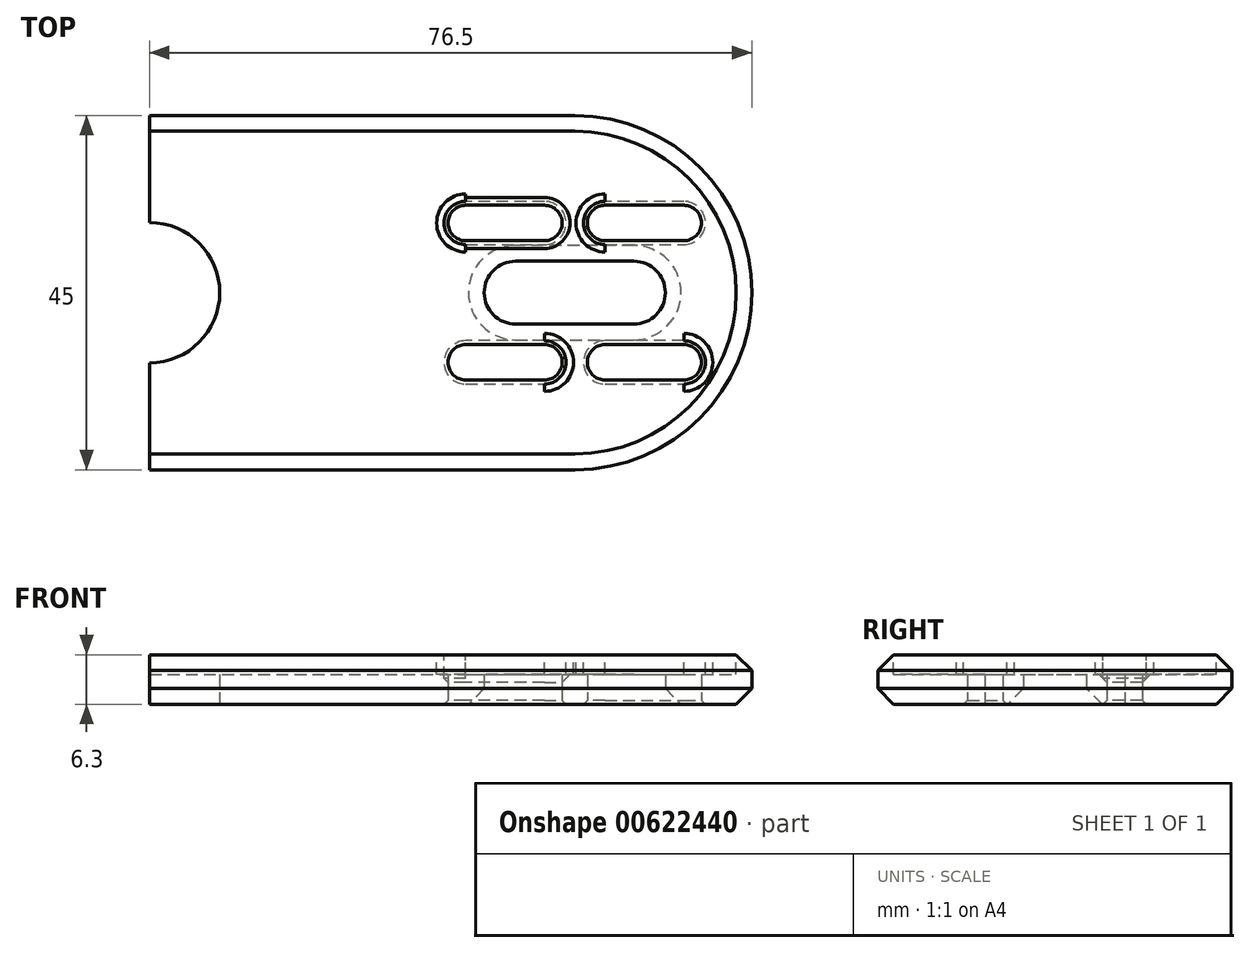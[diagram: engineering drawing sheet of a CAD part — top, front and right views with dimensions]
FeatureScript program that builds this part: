
annotation { "Feature Type Name" : "Feature", "Feature Type Description" : "" }
export const myFeature = defineFeature(function(context is Context, id is Id, definition is map)
    precondition{}
    {
        {
            var Q0;
            Q0=qCreatedBy(makeId("Top.planeOp"),FACE);
            var sketch = newSketch(context, id + "F0", { "sketchPlane" : qUnion([Q0])});
            skLineSegment(sketch, "E0.bottom", {"start": v(27, 22.5) * mm, "end": v(-27, 22.5) * mm});
            skLineSegment(sketch, "E0.top", {"start": v(27, -22.5) * mm, "end": v(-27, -22.5) * mm});
            skLineSegment(sketch, "E0.left", {"start": v(27, 22.5) * mm, "end": v(27, -22.5) * mm});
            skLineSegment(sketch, "E0.right", {"start": v(-27, 22.5) * mm, "end": v(-27, -22.5) * mm});
            skPoint(sketch, "E0.middle", {"position": v(0, 0) * mm});
            skArc(sketch, "E1", {"start": v(27, -22.5) * mm, "mid": v(49.5, 0) * mm, "end": v(27, 22.5) * mm});
            skArc(sketch, "E2", {"start": v(-27, -22.5) * mm, "mid": v(-49.5, 0) * mm, "end": v(-27, 22.5) * mm});
            skCircle(sketch, "E3", {"center": v(-27, 0) * mm, "radius": 8.9 * mm});
            skLineSegment(sketch, "E4.bottom", {"start": v(34.5, 4) * mm, "end": v(19.5, 4) * mm});
            skLineSegment(sketch, "E4.top", {"start": v(34.5, -4) * mm, "end": v(19.5, -4) * mm});
            skLineSegment(sketch, "E4.left", {"start": v(34.5, 4) * mm, "end": v(34.5, -4) * mm});
            skLineSegment(sketch, "E4.right", {"start": v(19.5, 4) * mm, "end": v(19.5, -4) * mm});
            skArc(sketch, "E5", {"start": v(34.5, -4) * mm, "mid": v(38.5, 0) * mm, "end": v(34.5, 4) * mm});
            skArc(sketch, "E6", {"start": v(19.5, -4) * mm, "mid": v(15.5, 0) * mm, "end": v(19.5, 4) * mm});
            skPoint(sketch, "E7.middle.positionSnap0", {"position": v(38.5, 0) * mm});
            skPoint(sketch, "E7.centerSnap0", {"position": v(38.5, 0) * mm});
            skPoint(sketch, "E8.middle.positionSnap0", {"position": v(15.5, 0) * mm});
            skPoint(sketch, "E8.centerSnap0", {"position": v(15.5, 0) * mm});
            skLineSegment(sketch, "E9.bottom", {"start": v(30.85, 11.1) * mm, "end": v(40.85, 11.1) * mm});
            skLineSegment(sketch, "E9.top", {"start": v(30.85, 6.6) * mm, "end": v(40.85, 6.6) * mm});
            skLineSegment(sketch, "E9.left", {"start": v(30.85, 11.1) * mm, "end": v(30.85, 6.6) * mm});
            skLineSegment(sketch, "E9.right", {"start": v(40.85, 11.1) * mm, "end": v(40.85, 6.6) * mm});
            skPoint(sketch, "E9.middle", {"position": v(35.85, 8.85) * mm});
            skLineSegment(sketch, "E10.bottom", {"start": v(13.15, 11.1) * mm, "end": v(23.15, 11.1) * mm});
            skLineSegment(sketch, "E10.top", {"start": v(13.15, 6.6) * mm, "end": v(23.15, 6.6) * mm});
            skLineSegment(sketch, "E10.left", {"start": v(13.15, 11.1) * mm, "end": v(13.15, 6.6) * mm});
            skLineSegment(sketch, "E10.right", {"start": v(23.15, 11.1) * mm, "end": v(23.15, 6.6) * mm});
            skPoint(sketch, "E10.middle", {"position": v(18.15, 8.85) * mm});
            skLineSegment(sketch, "E11.bottom", {"start": v(13.15, -11.1) * mm, "end": v(23.15, -11.1) * mm});
            skLineSegment(sketch, "E11.top", {"start": v(13.15, -6.6) * mm, "end": v(23.15, -6.6) * mm});
            skLineSegment(sketch, "E11.left", {"start": v(13.15, -11.1) * mm, "end": v(13.15, -6.6) * mm});
            skLineSegment(sketch, "E11.right", {"start": v(23.15, -11.1) * mm, "end": v(23.15, -6.6) * mm});
            skPoint(sketch, "E11.middle", {"position": v(18.15, -8.85) * mm});
            skLineSegment(sketch, "E12.bottom", {"start": v(30.85, -6.6) * mm, "end": v(40.85, -6.6) * mm});
            skLineSegment(sketch, "E12.top", {"start": v(30.85, -11.1) * mm, "end": v(40.85, -11.1) * mm});
            skLineSegment(sketch, "E12.left", {"start": v(30.85, -6.6) * mm, "end": v(30.85, -11.1) * mm});
            skLineSegment(sketch, "E12.right", {"start": v(40.85, -6.6) * mm, "end": v(40.85, -11.1) * mm});
            skPoint(sketch, "E12.middle", {"position": v(35.85, -8.85) * mm});
            skArc(sketch, "E13", {"start": v(13.15, 6.6) * mm, "mid": v(10.9, 8.85) * mm, "end": v(13.15, 11.1) * mm});
            skArc(sketch, "E14", {"start": v(23.15, 11.1) * mm, "mid": v(25.4, 8.85) * mm, "end": v(23.15, 6.6) * mm});
            skArc(sketch, "E15", {"start": v(30.85, 6.6) * mm, "mid": v(28.6, 8.85) * mm, "end": v(30.85, 11.1) * mm});
            skArc(sketch, "E16", {"start": v(40.85, 11.1) * mm, "mid": v(43.1, 8.85) * mm, "end": v(40.85, 6.6) * mm});
            skArc(sketch, "E17", {"start": v(23.15, -11.1) * mm, "mid": v(25.4, -8.85) * mm, "end": v(23.15, -6.6) * mm});
            skArc(sketch, "E18", {"start": v(13.15, -11.1) * mm, "mid": v(10.9, -8.85) * mm, "end": v(13.15, -6.6) * mm});
            skArc(sketch, "E19", {"start": v(30.85, -11.1) * mm, "mid": v(28.6, -8.85) * mm, "end": v(30.85, -6.6) * mm});
            skArc(sketch, "E20", {"start": v(40.85, -11.1) * mm, "mid": v(43.1, -8.85) * mm, "end": v(40.85, -6.6) * mm});
            skSolve(sketch);
        }
        {
            var Q0;
            {var subQ1=sQuery(id+"F0.wireOp",EDGE,"E1");Q0=makeQuery(id+"F0.imprint","IMPRINT",FACE,{"disambiguationData":[TD([[makeQuery(id+"F0.imprint","IMPRINT",EDGE,{"derivedFrom":subQ1}),1.0]])]});}
            var Q1;
            {var subQ6=sQuery(id+"F0.wireOp",EDGE,"E0.bottom");Q1=makeQuery(id+"F0.imprint","IMPRINT",FACE,{"disambiguationData":[TD([[makeQuery(id+"F0.imprint","IMPRINT",EDGE,{"derivedFrom":subQ6}),1.0]])]});}
            var Q2;
            {var subQ0=sQuery(id+"F0.wireOp",EDGE,"E2");Q2=makeQuery(id+"F0.imprint","IMPRINT",FACE,{"disambiguationData":[TD([[makeQuery(id+"F0.imprint","IMPRINT",EDGE,{"derivedFrom":subQ0}),-1.0]])]});}
            extrude(context, id + "F1", {"entities" : qUnion([Q0, Q1, Q2]), "depth" : 6.3 * mm, "offsetDistance" : 25 * mm});
        }
        {
            var Q0;
            Q0=makeQuery(id+"F1.opExtrude","CAP_EDGE",EDGE,{"disambiguationData":[OSD([sQuery(id+"F0.wireOp",EDGE,"E10.bottom")])],"isStart":false});
            var Q1;
            Q1=makeQuery(id+"F1.opExtrude","CAP_EDGE",EDGE,{"disambiguationData":[OSD([sQuery(id+"F0.wireOp",EDGE,"E9.bottom")])],"isStart":false});
            var Q2;
            Q2=makeQuery(id+"F1.opExtrude","CAP_EDGE",EDGE,{"disambiguationData":[OSD([sQuery(id+"F0.wireOp",EDGE,"E12.bottom")])],"isStart":false});
            var Q3;
            Q3=makeQuery(id+"F1.opExtrude","CAP_EDGE",EDGE,{"disambiguationData":[OSD([sQuery(id+"F0.wireOp",EDGE,"E11.top")])],"isStart":false});
            var Q4;
            Q4=makeQuery(id+"F1.opExtrude","CAP_EDGE",EDGE,{"disambiguationData":[OSD([sQuery(id+"F0.wireOp",EDGE,"E9.bottom")])],"isStart":true});
            var Q5;
            Q5=makeQuery(id+"F1.opExtrude","CAP_EDGE",EDGE,{"disambiguationData":[OSD([sQuery(id+"F0.wireOp",EDGE,"E10.bottom")])],"isStart":true});
            var Q6;
            Q6=makeQuery(id+"F1.opExtrude","CAP_EDGE",EDGE,{"disambiguationData":[OSD([sQuery(id+"F0.wireOp",EDGE,"E12.bottom")])],"isStart":true});
            var Q7;
            Q7=makeQuery(id+"F1.opExtrude","CAP_EDGE",EDGE,{"disambiguationData":[OSD([sQuery(id+"F0.wireOp",EDGE,"E11.top")])],"isStart":true});
            chamfer(context, id + "F2", {"entities" : qUnion([Q0, Q1, Q2, Q3, Q4, Q5, Q6, Q7]), "width" : .5 * mm, "tangentPropagation" : true});
        }
        {
            var Q0;
            Q0=makeQuery(id+"F1.opExtrude","CAP_EDGE",EDGE,{"disambiguationData":[OSD([sQuery(id+"F0.wireOp",EDGE,"E0.top")])],"isStart":false});
            var Q1;
            Q1=makeQuery(id+"F1.opExtrude","CAP_EDGE",EDGE,{"disambiguationData":[OSD([sQuery(id+"F0.wireOp",EDGE,"E0.top")])],"isStart":true});
            chamfer(context, id + "F3", {"entities" : qUnion([Q0, Q1]), "width" : 2 * mm, "tangentPropagation" : true});
        }
        {
            var Q0;
            Q0=makeQuery(id+"F1.opExtrude","CAP_FACE",FACE,{"disambiguationData":[OSD([sQuery(id+"F0.wireOp",EDGE,"E0.bottom"),sQuery(id+"F0.wireOp",EDGE,"E0.top"),sQuery(id+"F0.wireOp",EDGE,"E1"),sQuery(id+"F0.wireOp",EDGE,"E2"),sQuery(id+"F0.wireOp",EDGE,"E3"),sQuery(id+"F0.wireOp",EDGE,"E4.bottom"),sQuery(id+"F0.wireOp",EDGE,"E4.top"),sQuery(id+"F0.wireOp",EDGE,"E5"),sQuery(id+"F0.wireOp",EDGE,"E6"),sQuery(id+"F0.wireOp",EDGE,"E9.bottom"),sQuery(id+"F0.wireOp",EDGE,"E9.top"),sQuery(id+"F0.wireOp",EDGE,"E10.bottom"),sQuery(id+"F0.wireOp",EDGE,"E10.top"),sQuery(id+"F0.wireOp",EDGE,"E11.bottom"),sQuery(id+"F0.wireOp",EDGE,"E11.top"),sQuery(id+"F0.wireOp",EDGE,"E12.bottom"),sQuery(id+"F0.wireOp",EDGE,"E12.top"),sQuery(id+"F0.wireOp",EDGE,"E13"),sQuery(id+"F0.wireOp",EDGE,"E14"),sQuery(id+"F0.wireOp",EDGE,"E15"),sQuery(id+"F0.wireOp",EDGE,"E16"),sQuery(id+"F0.wireOp",EDGE,"E17"),sQuery(id+"F0.wireOp",EDGE,"E18"),sQuery(id+"F0.wireOp",EDGE,"E19"),sQuery(id+"F0.wireOp",EDGE,"E20")])],"isStart":false});
            var sketch = newSketch(context, id + "F4", { "sketchPlane" : qUnion([Q0])});
            skLineSegment(sketch, "E21.bottom", {"start": v(13.15, 12.54) * mm, "end": v(23.15, 12.54) * mm});
            skLineSegment(sketch, "E21.top", {"start": v(13.15, 5.16) * mm, "end": v(23.15, 5.16) * mm});
            skLineSegment(sketch, "E21.left", {"start": v(13.15, 12.54) * mm, "end": v(13.15, 5.16) * mm});
            skLineSegment(sketch, "E21.right", {"start": v(23.15, 12.54) * mm, "end": v(23.15, 5.16) * mm});
            skArc(sketch, "E22", {"start": v(13.15, 5.16) * mm, "mid": v(9.46, 8.85) * mm, "end": v(13.15, 12.54) * mm});
            skArc(sketch, "E23", {"start": v(23.15, 5.16) * mm, "mid": v(26.84, 8.85) * mm, "end": v(23.15, 12.54) * mm});
            skLineSegment(sketch, "E24.MirrorCS", {"start": v(40.85, 5.16) * mm, "end": v(30.85, 5.16) * mm});
            skLineSegment(sketch, "E25.MirrorCS", {"start": v(40.85, 12.54) * mm, "end": v(40.85, 5.16) * mm});
            skArc(sketch, "E26.MirrorCS", {"start": v(40.85, 5.16) * mm, "mid": v(44.54, 8.85) * mm, "end": v(40.85, 12.54) * mm});
            skArc(sketch, "E27.MirrorCS", {"start": v(30.85, 5.16) * mm, "mid": v(27.16, 8.85) * mm, "end": v(30.85, 12.54) * mm});
            skLineSegment(sketch, "E28.MirrorCS", {"start": v(40.85, 12.54) * mm, "end": v(30.85, 12.54) * mm});
            skLineSegment(sketch, "E29.MirrorCS", {"start": v(30.85, 12.54) * mm, "end": v(30.85, 5.16) * mm});
            skLineSegment(sketch, "E30.MirrorCS", {"start": v(40.85, -12.54) * mm, "end": v(40.85, -5.16) * mm});
            skLineSegment(sketch, "E31.MirrorCS", {"start": v(40.85, -12.54) * mm, "end": v(30.85, -12.54) * mm});
            skLineSegment(sketch, "E32.MirrorCS", {"start": v(23.15, -12.54) * mm, "end": v(23.15, -5.16) * mm});
            skLineSegment(sketch, "E33.MirrorCS", {"start": v(30.85, -12.54) * mm, "end": v(30.85, -5.16) * mm});
            skArc(sketch, "E34.MirrorCS", {"start": v(13.15, -5.16) * mm, "mid": v(9.46, -8.85) * mm, "end": v(13.15, -12.54) * mm});
            skLineSegment(sketch, "E35.MirrorCS", {"start": v(13.15, -12.54) * mm, "end": v(13.15, -5.16) * mm});
            skLineSegment(sketch, "E36.MirrorCS", {"start": v(13.15, -5.16) * mm, "end": v(23.15, -5.16) * mm});
            skArc(sketch, "E37.MirrorCS", {"start": v(40.85, -5.16) * mm, "mid": v(44.54, -8.85) * mm, "end": v(40.85, -12.54) * mm});
            skLineSegment(sketch, "E38.MirrorCS", {"start": v(40.85, -5.16) * mm, "end": v(30.85, -5.16) * mm});
            skLineSegment(sketch, "E39.MirrorCS", {"start": v(13.15, -12.54) * mm, "end": v(23.15, -12.54) * mm});
            skArc(sketch, "E40.MirrorCS", {"start": v(30.85, -5.16) * mm, "mid": v(27.16, -8.85) * mm, "end": v(30.85, -12.54) * mm});
            skArc(sketch, "E41.MirrorCS", {"start": v(23.15, -5.16) * mm, "mid": v(26.84, -8.85) * mm, "end": v(23.15, -12.54) * mm});
            skSolve(sketch);
        }
        {
            var Q0;
            {var subQ0=sQuery(id+"F4.wireOp",EDGE,"E21.bottom");Q0=makeQuery(id+"F4.imprint","IMPRINT",FACE,{"disambiguationData":[TD([[makeQuery(id+"F4.imprint","IMPRINT",EDGE,{"derivedFrom":subQ0}),-1.0]])]});}
            var Q1;
            {var subQ6=sQuery(id+"F4.wireOp",EDGE,"E22");Q1=makeQuery(id+"F4.imprint","IMPRINT",FACE,{"disambiguationData":[TD([[makeQuery(id+"F4.imprint","IMPRINT",EDGE,{"derivedFrom":subQ6}),-1.0]])]});}
            var Q2;
            {var subQ1=sQuery(id+"F0.wireOp",EDGE,"E13");var subQ2=sQuery(id+"F0.wireOp",EDGE,"E10.top");var subQ3=sQuery(id+"F0.wireOp",EDGE,"E10.bottom");var subQ4=makeQuery(id+"F1.opExtrude","CAP_FACE",FACE,{"disambiguationData":[OSD([sQuery(id+"F0.wireOp",EDGE,"E0.bottom"),sQuery(id+"F0.wireOp",EDGE,"E0.top"),sQuery(id+"F0.wireOp",EDGE,"E1"),sQuery(id+"F0.wireOp",EDGE,"E2"),sQuery(id+"F0.wireOp",EDGE,"E3"),sQuery(id+"F0.wireOp",EDGE,"E4.bottom"),sQuery(id+"F0.wireOp",EDGE,"E4.top"),sQuery(id+"F0.wireOp",EDGE,"E5"),sQuery(id+"F0.wireOp",EDGE,"E6"),sQuery(id+"F0.wireOp",EDGE,"E9.bottom"),sQuery(id+"F0.wireOp",EDGE,"E9.top"),subQ3,subQ2,sQuery(id+"F0.wireOp",EDGE,"E11.bottom"),sQuery(id+"F0.wireOp",EDGE,"E11.top"),sQuery(id+"F0.wireOp",EDGE,"E12.bottom"),sQuery(id+"F0.wireOp",EDGE,"E12.top"),subQ1,sQuery(id+"F0.wireOp",EDGE,"E14"),sQuery(id+"F0.wireOp",EDGE,"E15"),sQuery(id+"F0.wireOp",EDGE,"E16"),sQuery(id+"F0.wireOp",EDGE,"E17"),sQuery(id+"F0.wireOp",EDGE,"E18"),sQuery(id+"F0.wireOp",EDGE,"E19"),sQuery(id+"F0.wireOp",EDGE,"E20")])],"isStart":false});var subQ5=makeQuery(id+"F2.opChamfer","BLEND_EDGE",EDGE,{"blendedFrom":[makeQuery(id+"F1.opExtrude","CAP_EDGE",EDGE,{"disambiguationData":[OSD([subQ1])],"isStart":false}),subQ4],"blendedInto":[subQ4]});Q2=makeQuery(id+"F4.imprint","IMPRINT",FACE,{"disambiguationData":[TD([[makeQuery(id+"F4.imprint","IMPRINT",EDGE,{"derivedFrom":subQ5}),-1.0]])]});}
            var Q3;
            {var subQ1=sQuery(id+"F0.wireOp",EDGE,"E14");var subQ2=sQuery(id+"F0.wireOp",EDGE,"E13");var subQ3=sQuery(id+"F0.wireOp",EDGE,"E10.top");var subQ4=sQuery(id+"F0.wireOp",EDGE,"E10.bottom");var subQ5=makeQuery(id+"F1.opExtrude","CAP_FACE",FACE,{"disambiguationData":[OSD([sQuery(id+"F0.wireOp",EDGE,"E0.bottom"),sQuery(id+"F0.wireOp",EDGE,"E0.top"),sQuery(id+"F0.wireOp",EDGE,"E1"),sQuery(id+"F0.wireOp",EDGE,"E2"),sQuery(id+"F0.wireOp",EDGE,"E3"),sQuery(id+"F0.wireOp",EDGE,"E4.bottom"),sQuery(id+"F0.wireOp",EDGE,"E4.top"),sQuery(id+"F0.wireOp",EDGE,"E5"),sQuery(id+"F0.wireOp",EDGE,"E6"),sQuery(id+"F0.wireOp",EDGE,"E9.bottom"),sQuery(id+"F0.wireOp",EDGE,"E9.top"),subQ4,subQ3,sQuery(id+"F0.wireOp",EDGE,"E11.bottom"),sQuery(id+"F0.wireOp",EDGE,"E11.top"),sQuery(id+"F0.wireOp",EDGE,"E12.bottom"),sQuery(id+"F0.wireOp",EDGE,"E12.top"),subQ2,subQ1,sQuery(id+"F0.wireOp",EDGE,"E15"),sQuery(id+"F0.wireOp",EDGE,"E16"),sQuery(id+"F0.wireOp",EDGE,"E17"),sQuery(id+"F0.wireOp",EDGE,"E18"),sQuery(id+"F0.wireOp",EDGE,"E19"),sQuery(id+"F0.wireOp",EDGE,"E20")])],"isStart":false});var subQ7=makeQuery(id+"F2.opChamfer","BLEND_EDGE",EDGE,{"blendedFrom":[makeQuery(id+"F1.opExtrude","CAP_EDGE",EDGE,{"disambiguationData":[OSD([subQ4])],"isStart":false}),subQ5],"blendedInto":[subQ5]});Q3=makeQuery(id+"F4.imprint","IMPRINT",FACE,{"disambiguationData":[TD([[makeQuery(id+"F4.imprint","IMPRINT",EDGE,{"derivedFrom":subQ7}),-1.0]])]});}
            var Q4;
            {var subQ0=sQuery(id+"F4.wireOp",EDGE,"E21.top");Q4=makeQuery(id+"F4.imprint","IMPRINT",FACE,{"disambiguationData":[TD([[makeQuery(id+"F4.imprint","IMPRINT",EDGE,{"derivedFrom":subQ0}),1.0]])]});}
            var Q5;
            {var subQ1=sQuery(id+"F0.wireOp",EDGE,"E14");var subQ2=sQuery(id+"F0.wireOp",EDGE,"E10.top");var subQ3=sQuery(id+"F0.wireOp",EDGE,"E10.bottom");var subQ4=makeQuery(id+"F1.opExtrude","CAP_FACE",FACE,{"disambiguationData":[OSD([sQuery(id+"F0.wireOp",EDGE,"E0.bottom"),sQuery(id+"F0.wireOp",EDGE,"E0.top"),sQuery(id+"F0.wireOp",EDGE,"E1"),sQuery(id+"F0.wireOp",EDGE,"E2"),sQuery(id+"F0.wireOp",EDGE,"E3"),sQuery(id+"F0.wireOp",EDGE,"E4.bottom"),sQuery(id+"F0.wireOp",EDGE,"E4.top"),sQuery(id+"F0.wireOp",EDGE,"E5"),sQuery(id+"F0.wireOp",EDGE,"E6"),sQuery(id+"F0.wireOp",EDGE,"E9.bottom"),sQuery(id+"F0.wireOp",EDGE,"E9.top"),subQ3,subQ2,sQuery(id+"F0.wireOp",EDGE,"E11.bottom"),sQuery(id+"F0.wireOp",EDGE,"E11.top"),sQuery(id+"F0.wireOp",EDGE,"E12.bottom"),sQuery(id+"F0.wireOp",EDGE,"E12.top"),sQuery(id+"F0.wireOp",EDGE,"E13"),subQ1,sQuery(id+"F0.wireOp",EDGE,"E15"),sQuery(id+"F0.wireOp",EDGE,"E16"),sQuery(id+"F0.wireOp",EDGE,"E17"),sQuery(id+"F0.wireOp",EDGE,"E18"),sQuery(id+"F0.wireOp",EDGE,"E19"),sQuery(id+"F0.wireOp",EDGE,"E20")])],"isStart":false});var subQ5=makeQuery(id+"F2.opChamfer","BLEND_EDGE",EDGE,{"blendedFrom":[makeQuery(id+"F1.opExtrude","CAP_EDGE",EDGE,{"disambiguationData":[OSD([subQ1])],"isStart":false}),subQ4],"blendedInto":[subQ4]});Q5=makeQuery(id+"F4.imprint","IMPRINT",FACE,{"disambiguationData":[TD([[makeQuery(id+"F4.imprint","IMPRINT",EDGE,{"derivedFrom":subQ5}),-1.0]])]});}
            var Q6;
            {var subQ6=sQuery(id+"F4.wireOp",EDGE,"E23");Q6=makeQuery(id+"F4.imprint","IMPRINT",FACE,{"disambiguationData":[TD([[makeQuery(id+"F4.imprint","IMPRINT",EDGE,{"derivedFrom":subQ6}),1.0]])]});}
            var Q7;
            {var subQ0=sQuery(id+"F4.wireOp",EDGE,"E27.MirrorCS");Q7=makeQuery(id+"F4.imprint","IMPRINT",FACE,{"disambiguationData":[TD([[makeQuery(id+"F4.imprint","IMPRINT",EDGE,{"derivedFrom":subQ0}),-1.0]])]});}
            var Q8;
            {var subQ1=sQuery(id+"F0.wireOp",EDGE,"E15");var subQ2=sQuery(id+"F0.wireOp",EDGE,"E9.top");var subQ3=sQuery(id+"F0.wireOp",EDGE,"E9.bottom");var subQ4=makeQuery(id+"F1.opExtrude","CAP_FACE",FACE,{"disambiguationData":[OSD([sQuery(id+"F0.wireOp",EDGE,"E0.bottom"),sQuery(id+"F0.wireOp",EDGE,"E0.top"),sQuery(id+"F0.wireOp",EDGE,"E1"),sQuery(id+"F0.wireOp",EDGE,"E2"),sQuery(id+"F0.wireOp",EDGE,"E3"),sQuery(id+"F0.wireOp",EDGE,"E4.bottom"),sQuery(id+"F0.wireOp",EDGE,"E4.top"),sQuery(id+"F0.wireOp",EDGE,"E5"),sQuery(id+"F0.wireOp",EDGE,"E6"),subQ3,subQ2,sQuery(id+"F0.wireOp",EDGE,"E10.bottom"),sQuery(id+"F0.wireOp",EDGE,"E10.top"),sQuery(id+"F0.wireOp",EDGE,"E11.bottom"),sQuery(id+"F0.wireOp",EDGE,"E11.top"),sQuery(id+"F0.wireOp",EDGE,"E12.bottom"),sQuery(id+"F0.wireOp",EDGE,"E12.top"),sQuery(id+"F0.wireOp",EDGE,"E13"),sQuery(id+"F0.wireOp",EDGE,"E14"),subQ1,sQuery(id+"F0.wireOp",EDGE,"E16"),sQuery(id+"F0.wireOp",EDGE,"E17"),sQuery(id+"F0.wireOp",EDGE,"E18"),sQuery(id+"F0.wireOp",EDGE,"E19"),sQuery(id+"F0.wireOp",EDGE,"E20")])],"isStart":false});var subQ5=makeQuery(id+"F2.opChamfer","BLEND_EDGE",EDGE,{"blendedFrom":[makeQuery(id+"F1.opExtrude","CAP_EDGE",EDGE,{"disambiguationData":[OSD([subQ1])],"isStart":false}),subQ4],"blendedInto":[subQ4]});Q8=makeQuery(id+"F4.imprint","IMPRINT",FACE,{"disambiguationData":[TD([[makeQuery(id+"F4.imprint","IMPRINT",EDGE,{"derivedFrom":subQ5}),-1.0]])]});}
            var Q9;
            {var subQ1=sQuery(id+"F0.wireOp",EDGE,"E16");var subQ2=sQuery(id+"F0.wireOp",EDGE,"E15");var subQ3=sQuery(id+"F0.wireOp",EDGE,"E9.top");var subQ4=sQuery(id+"F0.wireOp",EDGE,"E9.bottom");var subQ5=makeQuery(id+"F1.opExtrude","CAP_FACE",FACE,{"disambiguationData":[OSD([sQuery(id+"F0.wireOp",EDGE,"E0.bottom"),sQuery(id+"F0.wireOp",EDGE,"E0.top"),sQuery(id+"F0.wireOp",EDGE,"E1"),sQuery(id+"F0.wireOp",EDGE,"E2"),sQuery(id+"F0.wireOp",EDGE,"E3"),sQuery(id+"F0.wireOp",EDGE,"E4.bottom"),sQuery(id+"F0.wireOp",EDGE,"E4.top"),sQuery(id+"F0.wireOp",EDGE,"E5"),sQuery(id+"F0.wireOp",EDGE,"E6"),subQ4,subQ3,sQuery(id+"F0.wireOp",EDGE,"E10.bottom"),sQuery(id+"F0.wireOp",EDGE,"E10.top"),sQuery(id+"F0.wireOp",EDGE,"E11.bottom"),sQuery(id+"F0.wireOp",EDGE,"E11.top"),sQuery(id+"F0.wireOp",EDGE,"E12.bottom"),sQuery(id+"F0.wireOp",EDGE,"E12.top"),sQuery(id+"F0.wireOp",EDGE,"E13"),sQuery(id+"F0.wireOp",EDGE,"E14"),subQ2,subQ1,sQuery(id+"F0.wireOp",EDGE,"E17"),sQuery(id+"F0.wireOp",EDGE,"E18"),sQuery(id+"F0.wireOp",EDGE,"E19"),sQuery(id+"F0.wireOp",EDGE,"E20")])],"isStart":false});var subQ7=makeQuery(id+"F2.opChamfer","BLEND_EDGE",EDGE,{"blendedFrom":[makeQuery(id+"F1.opExtrude","CAP_EDGE",EDGE,{"disambiguationData":[OSD([subQ4])],"isStart":false}),subQ5],"blendedInto":[subQ5]});Q9=makeQuery(id+"F4.imprint","IMPRINT",FACE,{"disambiguationData":[TD([[makeQuery(id+"F4.imprint","IMPRINT",EDGE,{"derivedFrom":subQ7}),-1.0]])]});}
            var Q10;
            {var subQ6=sQuery(id+"F4.wireOp",EDGE,"E28.MirrorCS");Q10=makeQuery(id+"F4.imprint","IMPRINT",FACE,{"disambiguationData":[TD([[makeQuery(id+"F4.imprint","IMPRINT",EDGE,{"derivedFrom":subQ6}),1.0]])]});}
            var Q11;
            {var subQ0=sQuery(id+"F4.wireOp",EDGE,"E24.MirrorCS");Q11=makeQuery(id+"F4.imprint","IMPRINT",FACE,{"disambiguationData":[TD([[makeQuery(id+"F4.imprint","IMPRINT",EDGE,{"derivedFrom":subQ0}),-1.0]])]});}
            var Q12;
            {var subQ6=sQuery(id+"F4.wireOp",EDGE,"E26.MirrorCS");Q12=makeQuery(id+"F4.imprint","IMPRINT",FACE,{"disambiguationData":[TD([[makeQuery(id+"F4.imprint","IMPRINT",EDGE,{"derivedFrom":subQ6}),1.0]])]});}
            var Q13;
            {var subQ1=sQuery(id+"F0.wireOp",EDGE,"E16");var subQ2=sQuery(id+"F0.wireOp",EDGE,"E9.top");var subQ3=sQuery(id+"F0.wireOp",EDGE,"E9.bottom");var subQ4=makeQuery(id+"F1.opExtrude","CAP_FACE",FACE,{"disambiguationData":[OSD([sQuery(id+"F0.wireOp",EDGE,"E0.bottom"),sQuery(id+"F0.wireOp",EDGE,"E0.top"),sQuery(id+"F0.wireOp",EDGE,"E1"),sQuery(id+"F0.wireOp",EDGE,"E2"),sQuery(id+"F0.wireOp",EDGE,"E3"),sQuery(id+"F0.wireOp",EDGE,"E4.bottom"),sQuery(id+"F0.wireOp",EDGE,"E4.top"),sQuery(id+"F0.wireOp",EDGE,"E5"),sQuery(id+"F0.wireOp",EDGE,"E6"),subQ3,subQ2,sQuery(id+"F0.wireOp",EDGE,"E10.bottom"),sQuery(id+"F0.wireOp",EDGE,"E10.top"),sQuery(id+"F0.wireOp",EDGE,"E11.bottom"),sQuery(id+"F0.wireOp",EDGE,"E11.top"),sQuery(id+"F0.wireOp",EDGE,"E12.bottom"),sQuery(id+"F0.wireOp",EDGE,"E12.top"),sQuery(id+"F0.wireOp",EDGE,"E13"),sQuery(id+"F0.wireOp",EDGE,"E14"),sQuery(id+"F0.wireOp",EDGE,"E15"),subQ1,sQuery(id+"F0.wireOp",EDGE,"E17"),sQuery(id+"F0.wireOp",EDGE,"E18"),sQuery(id+"F0.wireOp",EDGE,"E19"),sQuery(id+"F0.wireOp",EDGE,"E20")])],"isStart":false});var subQ5=makeQuery(id+"F2.opChamfer","BLEND_EDGE",EDGE,{"blendedFrom":[makeQuery(id+"F1.opExtrude","CAP_EDGE",EDGE,{"disambiguationData":[OSD([subQ1])],"isStart":false}),subQ4],"blendedInto":[subQ4]});Q13=makeQuery(id+"F4.imprint","IMPRINT",FACE,{"disambiguationData":[TD([[makeQuery(id+"F4.imprint","IMPRINT",EDGE,{"derivedFrom":subQ5}),-1.0]])]});}
            var Q14;
            {var subQ1=sQuery(id+"F0.wireOp",EDGE,"E18");var subQ2=sQuery(id+"F0.wireOp",EDGE,"E17");var subQ3=sQuery(id+"F0.wireOp",EDGE,"E11.top");var subQ4=sQuery(id+"F0.wireOp",EDGE,"E11.bottom");var subQ5=makeQuery(id+"F1.opExtrude","CAP_FACE",FACE,{"disambiguationData":[OSD([sQuery(id+"F0.wireOp",EDGE,"E0.bottom"),sQuery(id+"F0.wireOp",EDGE,"E0.top"),sQuery(id+"F0.wireOp",EDGE,"E1"),sQuery(id+"F0.wireOp",EDGE,"E2"),sQuery(id+"F0.wireOp",EDGE,"E3"),sQuery(id+"F0.wireOp",EDGE,"E4.bottom"),sQuery(id+"F0.wireOp",EDGE,"E4.top"),sQuery(id+"F0.wireOp",EDGE,"E5"),sQuery(id+"F0.wireOp",EDGE,"E6"),sQuery(id+"F0.wireOp",EDGE,"E9.bottom"),sQuery(id+"F0.wireOp",EDGE,"E9.top"),sQuery(id+"F0.wireOp",EDGE,"E10.bottom"),sQuery(id+"F0.wireOp",EDGE,"E10.top"),subQ4,subQ3,sQuery(id+"F0.wireOp",EDGE,"E12.bottom"),sQuery(id+"F0.wireOp",EDGE,"E12.top"),sQuery(id+"F0.wireOp",EDGE,"E13"),sQuery(id+"F0.wireOp",EDGE,"E14"),sQuery(id+"F0.wireOp",EDGE,"E15"),sQuery(id+"F0.wireOp",EDGE,"E16"),subQ2,subQ1,sQuery(id+"F0.wireOp",EDGE,"E19"),sQuery(id+"F0.wireOp",EDGE,"E20")])],"isStart":false});var subQ7=makeQuery(id+"F2.opChamfer","BLEND_EDGE",EDGE,{"blendedFrom":[makeQuery(id+"F1.opExtrude","CAP_EDGE",EDGE,{"disambiguationData":[OSD([subQ4])],"isStart":false}),subQ5],"blendedInto":[subQ5]});Q14=makeQuery(id+"F4.imprint","IMPRINT",FACE,{"disambiguationData":[TD([[makeQuery(id+"F4.imprint","IMPRINT",EDGE,{"derivedFrom":subQ7}),-1.0]])]});}
            var Q15;
            {var subQ1=sQuery(id+"F0.wireOp",EDGE,"E18");var subQ2=sQuery(id+"F0.wireOp",EDGE,"E11.top");var subQ3=sQuery(id+"F0.wireOp",EDGE,"E11.bottom");var subQ4=makeQuery(id+"F1.opExtrude","CAP_FACE",FACE,{"disambiguationData":[OSD([sQuery(id+"F0.wireOp",EDGE,"E0.bottom"),sQuery(id+"F0.wireOp",EDGE,"E0.top"),sQuery(id+"F0.wireOp",EDGE,"E1"),sQuery(id+"F0.wireOp",EDGE,"E2"),sQuery(id+"F0.wireOp",EDGE,"E3"),sQuery(id+"F0.wireOp",EDGE,"E4.bottom"),sQuery(id+"F0.wireOp",EDGE,"E4.top"),sQuery(id+"F0.wireOp",EDGE,"E5"),sQuery(id+"F0.wireOp",EDGE,"E6"),sQuery(id+"F0.wireOp",EDGE,"E9.bottom"),sQuery(id+"F0.wireOp",EDGE,"E9.top"),sQuery(id+"F0.wireOp",EDGE,"E10.bottom"),sQuery(id+"F0.wireOp",EDGE,"E10.top"),subQ3,subQ2,sQuery(id+"F0.wireOp",EDGE,"E12.bottom"),sQuery(id+"F0.wireOp",EDGE,"E12.top"),sQuery(id+"F0.wireOp",EDGE,"E13"),sQuery(id+"F0.wireOp",EDGE,"E14"),sQuery(id+"F0.wireOp",EDGE,"E15"),sQuery(id+"F0.wireOp",EDGE,"E16"),sQuery(id+"F0.wireOp",EDGE,"E17"),subQ1,sQuery(id+"F0.wireOp",EDGE,"E19"),sQuery(id+"F0.wireOp",EDGE,"E20")])],"isStart":false});var subQ5=makeQuery(id+"F2.opChamfer","BLEND_EDGE",EDGE,{"blendedFrom":[makeQuery(id+"F1.opExtrude","CAP_EDGE",EDGE,{"disambiguationData":[OSD([subQ1])],"isStart":false}),subQ4],"blendedInto":[subQ4]});Q15=makeQuery(id+"F4.imprint","IMPRINT",FACE,{"disambiguationData":[TD([[makeQuery(id+"F4.imprint","IMPRINT",EDGE,{"derivedFrom":subQ5}),-1.0]])]});}
            var Q16;
            {var subQ1=sQuery(id+"F0.wireOp",EDGE,"E17");var subQ2=sQuery(id+"F0.wireOp",EDGE,"E11.top");var subQ3=sQuery(id+"F0.wireOp",EDGE,"E11.bottom");var subQ4=makeQuery(id+"F1.opExtrude","CAP_FACE",FACE,{"disambiguationData":[OSD([sQuery(id+"F0.wireOp",EDGE,"E0.bottom"),sQuery(id+"F0.wireOp",EDGE,"E0.top"),sQuery(id+"F0.wireOp",EDGE,"E1"),sQuery(id+"F0.wireOp",EDGE,"E2"),sQuery(id+"F0.wireOp",EDGE,"E3"),sQuery(id+"F0.wireOp",EDGE,"E4.bottom"),sQuery(id+"F0.wireOp",EDGE,"E4.top"),sQuery(id+"F0.wireOp",EDGE,"E5"),sQuery(id+"F0.wireOp",EDGE,"E6"),sQuery(id+"F0.wireOp",EDGE,"E9.bottom"),sQuery(id+"F0.wireOp",EDGE,"E9.top"),sQuery(id+"F0.wireOp",EDGE,"E10.bottom"),sQuery(id+"F0.wireOp",EDGE,"E10.top"),subQ3,subQ2,sQuery(id+"F0.wireOp",EDGE,"E12.bottom"),sQuery(id+"F0.wireOp",EDGE,"E12.top"),sQuery(id+"F0.wireOp",EDGE,"E13"),sQuery(id+"F0.wireOp",EDGE,"E14"),sQuery(id+"F0.wireOp",EDGE,"E15"),sQuery(id+"F0.wireOp",EDGE,"E16"),subQ1,sQuery(id+"F0.wireOp",EDGE,"E18"),sQuery(id+"F0.wireOp",EDGE,"E19"),sQuery(id+"F0.wireOp",EDGE,"E20")])],"isStart":false});var subQ5=makeQuery(id+"F2.opChamfer","BLEND_EDGE",EDGE,{"blendedFrom":[makeQuery(id+"F1.opExtrude","CAP_EDGE",EDGE,{"disambiguationData":[OSD([subQ1])],"isStart":false}),subQ4],"blendedInto":[subQ4]});Q16=makeQuery(id+"F4.imprint","IMPRINT",FACE,{"disambiguationData":[TD([[makeQuery(id+"F4.imprint","IMPRINT",EDGE,{"derivedFrom":subQ5}),-1.0]])]});}
            var Q17;
            {var subQ6=sQuery(id+"F4.wireOp",EDGE,"E36.MirrorCS");Q17=makeQuery(id+"F4.imprint","IMPRINT",FACE,{"disambiguationData":[TD([[makeQuery(id+"F4.imprint","IMPRINT",EDGE,{"derivedFrom":subQ6}),-1.0]])]});}
            var Q18;
            {var subQ6=sQuery(id+"F4.wireOp",EDGE,"E41.MirrorCS");Q18=makeQuery(id+"F4.imprint","IMPRINT",FACE,{"disambiguationData":[TD([[makeQuery(id+"F4.imprint","IMPRINT",EDGE,{"derivedFrom":subQ6}),-1.0]])]});}
            var Q19;
            {var subQ6=sQuery(id+"F4.wireOp",EDGE,"E39.MirrorCS");Q19=makeQuery(id+"F4.imprint","IMPRINT",FACE,{"disambiguationData":[TD([[makeQuery(id+"F4.imprint","IMPRINT",EDGE,{"derivedFrom":subQ6}),1.0]])]});}
            var Q20;
            {var subQ0=sQuery(id+"F4.wireOp",EDGE,"E34.MirrorCS");Q20=makeQuery(id+"F4.imprint","IMPRINT",FACE,{"disambiguationData":[TD([[makeQuery(id+"F4.imprint","IMPRINT",EDGE,{"derivedFrom":subQ0}),1.0]])]});}
            var Q21;
            {var subQ6=sQuery(id+"F4.wireOp",EDGE,"E40.MirrorCS");Q21=makeQuery(id+"F4.imprint","IMPRINT",FACE,{"disambiguationData":[TD([[makeQuery(id+"F4.imprint","IMPRINT",EDGE,{"derivedFrom":subQ6}),1.0]])]});}
            var Q22;
            {var subQ6=sQuery(id+"F4.wireOp",EDGE,"E38.MirrorCS");Q22=makeQuery(id+"F4.imprint","IMPRINT",FACE,{"disambiguationData":[TD([[makeQuery(id+"F4.imprint","IMPRINT",EDGE,{"derivedFrom":subQ6}),1.0]])]});}
            var Q23;
            {var subQ1=sQuery(id+"F0.wireOp",EDGE,"E20");var subQ2=sQuery(id+"F0.wireOp",EDGE,"E19");var subQ3=sQuery(id+"F0.wireOp",EDGE,"E12.top");var subQ4=sQuery(id+"F0.wireOp",EDGE,"E12.bottom");var subQ5=makeQuery(id+"F1.opExtrude","CAP_FACE",FACE,{"disambiguationData":[OSD([sQuery(id+"F0.wireOp",EDGE,"E0.bottom"),sQuery(id+"F0.wireOp",EDGE,"E0.top"),sQuery(id+"F0.wireOp",EDGE,"E1"),sQuery(id+"F0.wireOp",EDGE,"E2"),sQuery(id+"F0.wireOp",EDGE,"E3"),sQuery(id+"F0.wireOp",EDGE,"E4.bottom"),sQuery(id+"F0.wireOp",EDGE,"E4.top"),sQuery(id+"F0.wireOp",EDGE,"E5"),sQuery(id+"F0.wireOp",EDGE,"E6"),sQuery(id+"F0.wireOp",EDGE,"E9.bottom"),sQuery(id+"F0.wireOp",EDGE,"E9.top"),sQuery(id+"F0.wireOp",EDGE,"E10.bottom"),sQuery(id+"F0.wireOp",EDGE,"E10.top"),sQuery(id+"F0.wireOp",EDGE,"E11.bottom"),sQuery(id+"F0.wireOp",EDGE,"E11.top"),subQ4,subQ3,sQuery(id+"F0.wireOp",EDGE,"E13"),sQuery(id+"F0.wireOp",EDGE,"E14"),sQuery(id+"F0.wireOp",EDGE,"E15"),sQuery(id+"F0.wireOp",EDGE,"E16"),sQuery(id+"F0.wireOp",EDGE,"E17"),sQuery(id+"F0.wireOp",EDGE,"E18"),subQ2,subQ1])],"isStart":false});var subQ7=makeQuery(id+"F2.opChamfer","BLEND_EDGE",EDGE,{"blendedFrom":[makeQuery(id+"F1.opExtrude","CAP_EDGE",EDGE,{"disambiguationData":[OSD([subQ4])],"isStart":false}),subQ5],"blendedInto":[subQ5]});Q23=makeQuery(id+"F4.imprint","IMPRINT",FACE,{"disambiguationData":[TD([[makeQuery(id+"F4.imprint","IMPRINT",EDGE,{"derivedFrom":subQ7}),-1.0]])]});}
            var Q24;
            {var subQ6=sQuery(id+"F4.wireOp",EDGE,"E31.MirrorCS");Q24=makeQuery(id+"F4.imprint","IMPRINT",FACE,{"disambiguationData":[TD([[makeQuery(id+"F4.imprint","IMPRINT",EDGE,{"derivedFrom":subQ6}),-1.0]])]});}
            var Q25;
            {var subQ1=sQuery(id+"F0.wireOp",EDGE,"E19");var subQ2=sQuery(id+"F0.wireOp",EDGE,"E12.top");var subQ3=sQuery(id+"F0.wireOp",EDGE,"E12.bottom");var subQ4=makeQuery(id+"F1.opExtrude","CAP_FACE",FACE,{"disambiguationData":[OSD([sQuery(id+"F0.wireOp",EDGE,"E0.bottom"),sQuery(id+"F0.wireOp",EDGE,"E0.top"),sQuery(id+"F0.wireOp",EDGE,"E1"),sQuery(id+"F0.wireOp",EDGE,"E2"),sQuery(id+"F0.wireOp",EDGE,"E3"),sQuery(id+"F0.wireOp",EDGE,"E4.bottom"),sQuery(id+"F0.wireOp",EDGE,"E4.top"),sQuery(id+"F0.wireOp",EDGE,"E5"),sQuery(id+"F0.wireOp",EDGE,"E6"),sQuery(id+"F0.wireOp",EDGE,"E9.bottom"),sQuery(id+"F0.wireOp",EDGE,"E9.top"),sQuery(id+"F0.wireOp",EDGE,"E10.bottom"),sQuery(id+"F0.wireOp",EDGE,"E10.top"),sQuery(id+"F0.wireOp",EDGE,"E11.bottom"),sQuery(id+"F0.wireOp",EDGE,"E11.top"),subQ3,subQ2,sQuery(id+"F0.wireOp",EDGE,"E13"),sQuery(id+"F0.wireOp",EDGE,"E14"),sQuery(id+"F0.wireOp",EDGE,"E15"),sQuery(id+"F0.wireOp",EDGE,"E16"),sQuery(id+"F0.wireOp",EDGE,"E17"),sQuery(id+"F0.wireOp",EDGE,"E18"),subQ1,sQuery(id+"F0.wireOp",EDGE,"E20")])],"isStart":false});var subQ5=makeQuery(id+"F2.opChamfer","BLEND_EDGE",EDGE,{"blendedFrom":[makeQuery(id+"F1.opExtrude","CAP_EDGE",EDGE,{"disambiguationData":[OSD([subQ1])],"isStart":false}),subQ4],"blendedInto":[subQ4]});Q25=makeQuery(id+"F4.imprint","IMPRINT",FACE,{"disambiguationData":[TD([[makeQuery(id+"F4.imprint","IMPRINT",EDGE,{"derivedFrom":subQ5}),-1.0]])]});}
            var Q26;
            {var subQ1=sQuery(id+"F0.wireOp",EDGE,"E20");var subQ2=sQuery(id+"F0.wireOp",EDGE,"E12.top");var subQ3=sQuery(id+"F0.wireOp",EDGE,"E12.bottom");var subQ4=makeQuery(id+"F1.opExtrude","CAP_FACE",FACE,{"disambiguationData":[OSD([sQuery(id+"F0.wireOp",EDGE,"E0.bottom"),sQuery(id+"F0.wireOp",EDGE,"E0.top"),sQuery(id+"F0.wireOp",EDGE,"E1"),sQuery(id+"F0.wireOp",EDGE,"E2"),sQuery(id+"F0.wireOp",EDGE,"E3"),sQuery(id+"F0.wireOp",EDGE,"E4.bottom"),sQuery(id+"F0.wireOp",EDGE,"E4.top"),sQuery(id+"F0.wireOp",EDGE,"E5"),sQuery(id+"F0.wireOp",EDGE,"E6"),sQuery(id+"F0.wireOp",EDGE,"E9.bottom"),sQuery(id+"F0.wireOp",EDGE,"E9.top"),sQuery(id+"F0.wireOp",EDGE,"E10.bottom"),sQuery(id+"F0.wireOp",EDGE,"E10.top"),sQuery(id+"F0.wireOp",EDGE,"E11.bottom"),sQuery(id+"F0.wireOp",EDGE,"E11.top"),subQ3,subQ2,sQuery(id+"F0.wireOp",EDGE,"E13"),sQuery(id+"F0.wireOp",EDGE,"E14"),sQuery(id+"F0.wireOp",EDGE,"E15"),sQuery(id+"F0.wireOp",EDGE,"E16"),sQuery(id+"F0.wireOp",EDGE,"E17"),sQuery(id+"F0.wireOp",EDGE,"E18"),sQuery(id+"F0.wireOp",EDGE,"E19"),subQ1])],"isStart":false});var subQ5=makeQuery(id+"F2.opChamfer","BLEND_EDGE",EDGE,{"blendedFrom":[makeQuery(id+"F1.opExtrude","CAP_EDGE",EDGE,{"disambiguationData":[OSD([subQ1])],"isStart":false}),subQ4],"blendedInto":[subQ4]});Q26=makeQuery(id+"F4.imprint","IMPRINT",FACE,{"disambiguationData":[TD([[makeQuery(id+"F4.imprint","IMPRINT",EDGE,{"derivedFrom":subQ5}),-1.0]])]});}
            var Q27;
            {var subQ6=sQuery(id+"F4.wireOp",EDGE,"E37.MirrorCS");Q27=makeQuery(id+"F4.imprint","IMPRINT",FACE,{"disambiguationData":[TD([[makeQuery(id+"F4.imprint","IMPRINT",EDGE,{"derivedFrom":subQ6}),-1.0]])]});}
            extrude(context, id + "F5", {"entities" : qUnion([Q0, Q1, Q2, Q3, Q4, Q5, Q6, Q7, Q8, Q9, Q10, Q11, Q12, Q13, Q14, Q15, Q16, Q17, Q18, Q19, Q20, Q21, Q22, Q23, Q24, Q25, Q26, Q27]), "operationType" : NewBodyOperationType.REMOVE, "oppositeDirection" : true, "depth" : 2.5 * mm, "offsetDistance" : 25 * mm});
        }
        {
            var Q0;
            Q0=makeQuery(id+"F5.boolean.opBoolean","INTERSECT",EDGE,{"derivedFrom":[makeQuery(id+"F1.opExtrude","SWEPT_FACE",FACE,{"disambiguationData":[OSD([sQuery(id+"F0.wireOp",EDGE,"E13")])]}),makeQuery(id+"F5.opExtrude","CAP_FACE",FACE,{"disambiguationData":[OSD([sQuery(id+"F4.wireOp",EDGE,"E21.bottom"),sQuery(id+"F4.wireOp",EDGE,"E21.top"),sQuery(id+"F4.wireOp",EDGE,"E22"),sQuery(id+"F4.wireOp",EDGE,"E23")])],"isStart":false})]});
            var Q1;
            Q1=makeQuery(id+"F5.boolean.opBoolean","INTERSECT",EDGE,{"derivedFrom":[makeQuery(id+"F1.opExtrude","SWEPT_FACE",FACE,{"disambiguationData":[OSD([sQuery(id+"F0.wireOp",EDGE,"E10.top")])]}),makeQuery(id+"F5.opExtrude","CAP_FACE",FACE,{"disambiguationData":[OSD([sQuery(id+"F4.wireOp",EDGE,"E21.bottom"),sQuery(id+"F4.wireOp",EDGE,"E21.top"),sQuery(id+"F4.wireOp",EDGE,"E22"),sQuery(id+"F4.wireOp",EDGE,"E23")])],"isStart":false})]});
            var Q2;
            Q2=makeQuery(id+"F5.boolean.opBoolean","INTERSECT",EDGE,{"derivedFrom":[makeQuery(id+"F1.opExtrude","SWEPT_FACE",FACE,{"disambiguationData":[OSD([sQuery(id+"F0.wireOp",EDGE,"E14")])]}),makeQuery(id+"F5.opExtrude","CAP_FACE",FACE,{"disambiguationData":[OSD([sQuery(id+"F4.wireOp",EDGE,"E21.bottom"),sQuery(id+"F4.wireOp",EDGE,"E21.top"),sQuery(id+"F4.wireOp",EDGE,"E22"),sQuery(id+"F4.wireOp",EDGE,"E23")])],"isStart":false})]});
            var Q3;
            Q3=makeQuery(id+"F5.boolean.opBoolean","INTERSECT",EDGE,{"derivedFrom":[makeQuery(id+"F1.opExtrude","SWEPT_FACE",FACE,{"disambiguationData":[OSD([sQuery(id+"F0.wireOp",EDGE,"E10.bottom")])]}),makeQuery(id+"F5.opExtrude","CAP_FACE",FACE,{"disambiguationData":[OSD([sQuery(id+"F4.wireOp",EDGE,"E21.bottom"),sQuery(id+"F4.wireOp",EDGE,"E21.top"),sQuery(id+"F4.wireOp",EDGE,"E22"),sQuery(id+"F4.wireOp",EDGE,"E23")])],"isStart":false})]});
            var Q4;
            Q4=makeQuery(id+"F5.boolean.opBoolean","INTERSECT",EDGE,{"derivedFrom":[makeQuery(id+"F1.opExtrude","SWEPT_FACE",FACE,{"disambiguationData":[OSD([sQuery(id+"F0.wireOp",EDGE,"E11.top")])]}),makeQuery(id+"F5.opExtrude","CAP_FACE",FACE,{"disambiguationData":[OSD([sQuery(id+"F4.wireOp",EDGE,"60f98419-ae76-4f44-b9a4-ef226f25e08d1.MirrorCS"),sQuery(id+"F4.wireOp",EDGE,"60f98419-ae76-4f44-b9a4-ef226f25e08d4.MirrorCS"),sQuery(id+"F4.wireOp",EDGE,"60f98419-ae76-4f44-b9a4-ef226f25e08d10.MirrorCS"),sQuery(id+"F4.wireOp",EDGE,"60f98419-ae76-4f44-b9a4-ef226f25e08d11.MirrorCS")])],"isStart":false})]});
            var Q5;
            Q5=makeQuery(id+"F5.boolean.opBoolean","INTERSECT",EDGE,{"derivedFrom":[makeQuery(id+"F1.opExtrude","SWEPT_FACE",FACE,{"disambiguationData":[OSD([sQuery(id+"F0.wireOp",EDGE,"E12.bottom")])]}),makeQuery(id+"F5.opExtrude","CAP_FACE",FACE,{"disambiguationData":[OSD([sQuery(id+"F4.wireOp",EDGE,"60f98419-ae76-4f44-b9a4-ef226f25e08d2.MirrorCS"),sQuery(id+"F4.wireOp",EDGE,"60f98419-ae76-4f44-b9a4-ef226f25e08d6.MirrorCS"),sQuery(id+"F4.wireOp",EDGE,"60f98419-ae76-4f44-b9a4-ef226f25e08d7.MirrorCS"),sQuery(id+"F4.wireOp",EDGE,"60f98419-ae76-4f44-b9a4-ef226f25e08d9.MirrorCS")])],"isStart":false})]});
            var Q6;
            Q6=makeQuery(id+"F5.boolean.opBoolean","INTERSECT",EDGE,{"derivedFrom":[makeQuery(id+"F1.opExtrude","SWEPT_FACE",FACE,{"disambiguationData":[OSD([sQuery(id+"F0.wireOp",EDGE,"E9.bottom")])]}),makeQuery(id+"F5.opExtrude","CAP_FACE",FACE,{"disambiguationData":[OSD([sQuery(id+"F4.wireOp",EDGE,"eb5bfaa3-b50e-47f4-8079-7c7d18d66fb70.MirrorCS"),sQuery(id+"F4.wireOp",EDGE,"eb5bfaa3-b50e-47f4-8079-7c7d18d66fb73.MirrorCS"),sQuery(id+"F4.wireOp",EDGE,"99e5f55f-7cb7-4ef8-bb96-976eb3610d550.MirrorCS"),sQuery(id+"F4.wireOp",EDGE,"f2b48aa8-14ee-4420-a9c2-0b006843bb750.MirrorCS")])],"isStart":false})]});
            chamfer(context, id + "F6", {"entities" : qUnion([Q0, Q1, Q2, Q3, Q4, Q5, Q6]), "width" : 1 * mm, "tangentPropagation" : true});
        }
        {
            var Q0;
            Q0=makeQuery(id+"F1.opExtrude","CAP_EDGE",EDGE,{"disambiguationData":[OSD([sQuery(id+"F0.wireOp",EDGE,"E4.bottom")])],"isStart":true});
            chamfer(context, id + "F7", {"entities" : qUnion([Q0]), "width" : 2 * mm, "tangentPropagation" : true});
        }
    });
